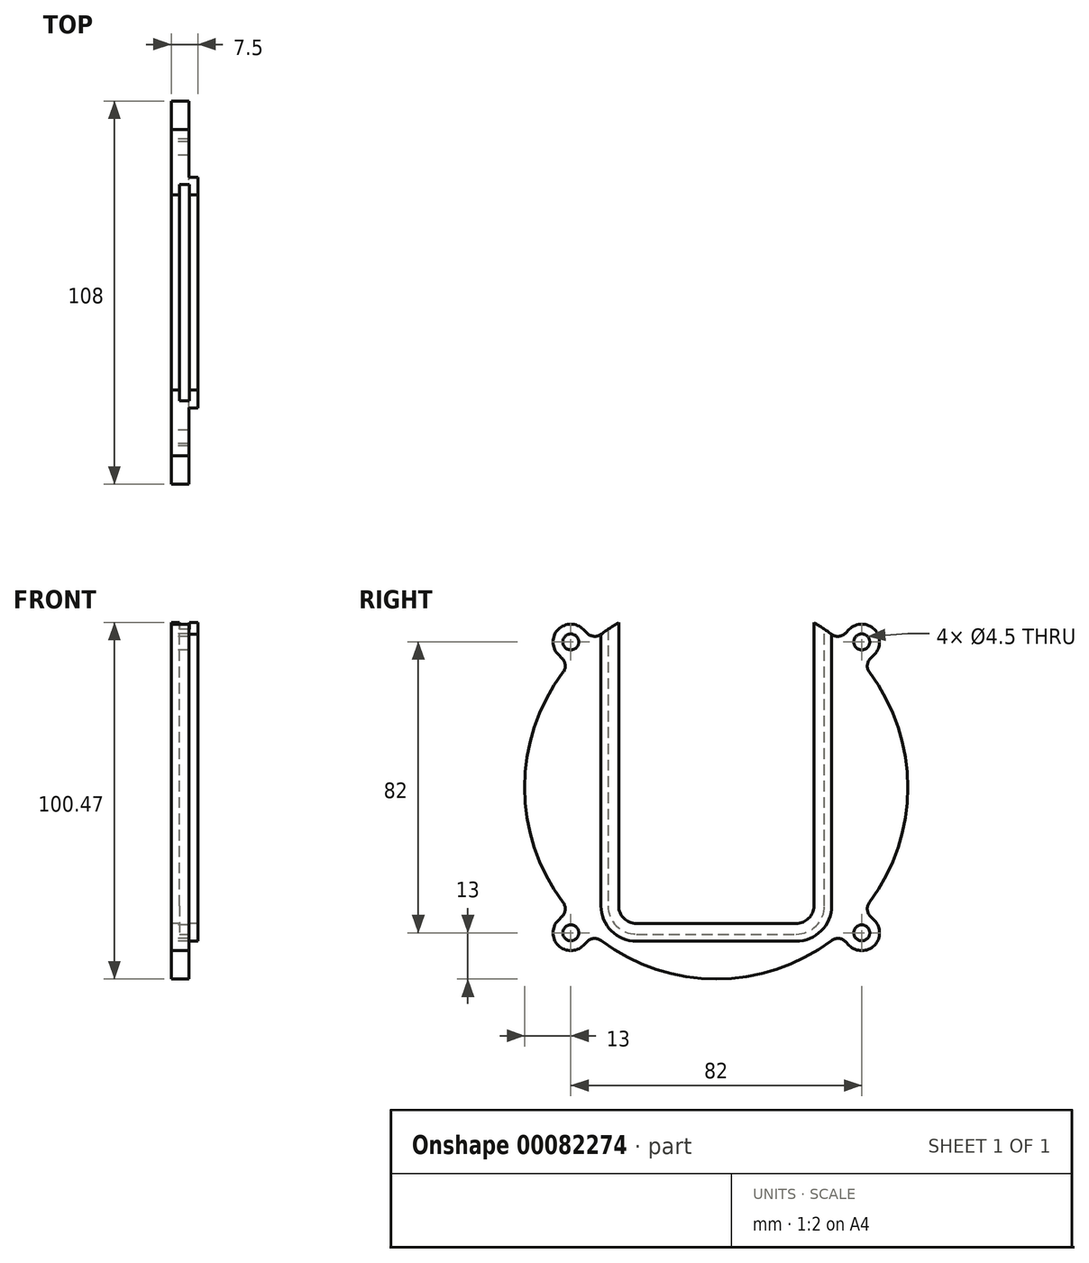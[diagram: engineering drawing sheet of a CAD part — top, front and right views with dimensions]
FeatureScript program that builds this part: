
annotation { "Feature Type Name" : "Feature", "Feature Type Description" : "" }
export const myFeature = defineFeature(function(context is Context, id is Id, definition is map)
    precondition{}
    {
        {
            var Q0;
            Q0=qCreatedBy(makeId("Right.planeOp"),FACE);
            var sketch = newSketch(context, id + "F0", { "sketchPlane" : qUnion([Q0])});
            skCircle(sketch, "E0", {"center": v(-41, 41) * mm, "radius": 2.25 * mm});
            skCircle(sketch, "E1", {"center": v(41, 41) * mm, "radius": 2.25 * mm});
            skCircle(sketch, "E2", {"center": v(41, -41) * mm, "radius": 2.25 * mm});
            skCircle(sketch, "E3", {"center": v(-41, -41) * mm, "radius": 2.25 * mm});
            skArc(sketch, "E4", {"start": v(-32.45, 43.16) * mm, "mid": v(-24.12, -48.31) * mm, "end": v(54, 0) * mm});
            skArc(sketch, "E5", {"start": v(37.46, -44.54) * mm, "mid": v(44.54, -44.54) * mm, "end": v(44.54, -37.46) * mm});
            skArc(sketch, "E6", {"start": v(-44.54, -37.46) * mm, "mid": v(-44.54, -44.54) * mm, "end": v(-37.46, -44.54) * mm});
            skLineSegment(sketch, "E7", {"start": v(-44.54, 37.46) * mm, "end": v(-36.42, 45.58) * mm, "construction": true});
            skLineSegment(sketch, "E8", {"start": v(-44.54, 37.46) * mm, "end": v(-43.44, 36.37) * mm});
            skLineSegment(sketch, "E9", {"start": v(-37.46, 44.54) * mm, "end": v(-36.37, 43.44) * mm});
            skLineSegment(sketch, "E10", {"start": v(37.46, 44.54) * mm, "end": v(46.12, 35.88) * mm, "construction": true});
            skLineSegment(sketch, "E11", {"start": v(37.46, 44.54) * mm, "end": v(36.37, 43.44) * mm});
            skLineSegment(sketch, "E12", {"start": v(44.54, 37.46) * mm, "end": v(43.44, 36.37) * mm});
            skLineSegment(sketch, "E13", {"start": v(-44.54, -37.46) * mm, "end": v(-35.54, -46.46) * mm, "construction": true});
            skLineSegment(sketch, "E14", {"start": v(-44.54, -37.46) * mm, "end": v(-43.44, -36.37) * mm});
            skLineSegment(sketch, "E15", {"start": v(-37.46, -44.54) * mm, "end": v(-36.37, -43.44) * mm});
            skLineSegment(sketch, "E16", {"start": v(37.46, -44.54) * mm, "end": v(47.36, -34.64) * mm, "construction": true});
            skLineSegment(sketch, "E17", {"start": v(37.46, -44.54) * mm, "end": v(36.37, -43.44) * mm});
            skLineSegment(sketch, "E18", {"start": v(44.54, -37.46) * mm, "end": v(43.44, -36.37) * mm});
            skArc(sketch, "E19.trimOffspring", {"start": v(-37.46, 44.54) * mm, "mid": v(-44.54, 44.54) * mm, "end": v(-44.54, 37.46) * mm});
            skArc(sketch, "E20.trimOffspring", {"start": v(32.45, 43.16) * mm, "mid": v(30.02, 44.89) * mm, "end": v(27.5, 46.47) * mm});
            skArc(sketch, "E21.trimOffspring", {"start": v(44.54, 37.46) * mm, "mid": v(44.54, 44.54) * mm, "end": v(37.46, 44.54) * mm});
            skArc(sketch, "E22.trimOffspring", {"start": v(-32.45, -43.16) * mm, "mid": v(0, -54) * mm, "end": v(32.45, -43.16) * mm});
            skPoint(sketch, "E23.visualSharp", {"position": v(-41.56, 34.48) * mm});
            skPoint(sketch, "E24.visualSharp", {"position": v(-34.48, 41.56) * mm});
            skArc(sketch, "E24.filletArc", {"start": v(-36.37, 43.44) * mm, "mid": v(-34.46, 42.57) * mm, "end": v(-32.45, 43.16) * mm});
            skPoint(sketch, "E25.visualSharp", {"position": v(-41.56, -34.48) * mm});
            skArc(sketch, "E25.filletArc", {"start": v(-43.44, -36.37) * mm, "mid": v(-42.57, -34.46) * mm, "end": v(-43.16, -32.45) * mm});
            skPoint(sketch, "E26.visualSharp", {"position": v(-34.48, -41.56) * mm});
            skArc(sketch, "E26.filletArc", {"start": v(-32.45, -43.16) * mm, "mid": v(-34.46, -42.57) * mm, "end": v(-36.37, -43.44) * mm});
            skPoint(sketch, "E27.visualSharp", {"position": v(41.56, -34.48) * mm});
            skArc(sketch, "E27.filletArc", {"start": v(43.16, -32.45) * mm, "mid": v(42.57, -34.46) * mm, "end": v(43.44, -36.37) * mm});
            skPoint(sketch, "E28.visualSharp", {"position": v(34.48, -41.56) * mm});
            skArc(sketch, "E28.filletArc", {"start": v(36.37, -43.44) * mm, "mid": v(34.46, -42.57) * mm, "end": v(32.45, -43.16) * mm});
            skPoint(sketch, "E29.visualSharp", {"position": v(41.56, 34.48) * mm});
            skArc(sketch, "E29.filletArc", {"start": v(43.44, 36.37) * mm, "mid": v(42.57, 34.46) * mm, "end": v(43.16, 32.45) * mm});
            skPoint(sketch, "E30.visualSharp", {"position": v(34.48, 41.56) * mm});
            skArc(sketch, "E30.filletArc", {"start": v(32.45, 43.16) * mm, "mid": v(34.46, 42.57) * mm, "end": v(36.37, 43.44) * mm});
            skArc(sketch, "E31.filletArc", {"start": v(-43.16, 32.45) * mm, "mid": v(-42.57, 34.46) * mm, "end": v(-43.44, 36.37) * mm});
            skArc(sketch, "E32.converted", {"start": v(-27.5, 46.47) * mm, "mid": v(0, -54) * mm, "end": v(27.5, 46.47) * mm});
            skLineSegment(sketch, "E33", {"start": v(-27.5, 46.47) * mm, "end": v(-27.5, -33.36) * mm});
            skLineSegment(sketch, "E34", {"start": v(27.5, 46.47) * mm, "end": v(27.5, -33.36) * mm});
            skCircle(sketch, "E35", {"center": v(0, 0) * mm, "radius": 17.5 * mm, "construction": true});
            skCircle(sketch, "E36", {"center": v(20.15, 20.15) * mm, "radius": 2.25 * mm, "construction": true});
            skCircle(sketch, "E37", {"center": v(-20.15, -20.15) * mm, "radius": 2.25 * mm, "construction": true});
            skLineSegment(sketch, "E38.bottom", {"start": v(-26.5, 26.5) * mm, "end": v(26.5, 26.5) * mm, "construction": true});
            skLineSegment(sketch, "E38.top", {"start": v(-26.5, -26.5) * mm, "end": v(26.5, -26.5) * mm, "construction": true});
            skLineSegment(sketch, "E38.left", {"start": v(-26.5, 26.5) * mm, "end": v(-26.5, -26.5) * mm, "construction": true});
            skLineSegment(sketch, "E38.right", {"start": v(26.5, 26.5) * mm, "end": v(26.5, -26.5) * mm, "construction": true});
            skArc(sketch, "E39.trimOffspring", {"start": v(-21.68, -18.5) * mm, "mid": v(-20.15, -20.15) * mm, "end": v(-18.5, -21.68) * mm, "construction": true});
            skArc(sketch, "E40.trimOffspring", {"start": v(21.68, 18.5) * mm, "mid": v(20.15, 20.15) * mm, "end": v(18.5, 21.68) * mm, "construction": true});
            skLineSegment(sketch, "E41", {"start": v(-22.5, -38.36) * mm, "end": v(22.5, -38.36) * mm});
            skPoint(sketch, "E42.orphan", {"position": v(-27.5, -21.94) * mm});
            skPoint(sketch, "E43.orphan", {"position": v(27.5, -21.94) * mm});
            skPoint(sketch, "E44.visualSharp", {"position": v(-27.5, -38.36) * mm});
            skArc(sketch, "E44.filletArc", {"start": v(-27.5, -33.36) * mm, "mid": v(-26.04, -36.9) * mm, "end": v(-22.5, -38.36) * mm});
            skPoint(sketch, "E45.visualSharp", {"position": v(27.5, -38.36) * mm});
            skArc(sketch, "E45.filletArc", {"start": v(22.5, -38.36) * mm, "mid": v(26.04, -36.9) * mm, "end": v(27.5, -33.36) * mm});
            skArc(sketch, "E46.trimOffspring", {"start": v(-27.5, 46.47) * mm, "mid": v(-30.02, 44.89) * mm, "end": v(-32.45, 43.16) * mm});
            skPoint(sketch, "E47.orphan", {"position": v(-27.5, 53.27) * mm});
            skPoint(sketch, "E48.orphan", {"position": v(27.5, 53.27) * mm});
            skLineSegment(sketch, "E49", {"start": v(-32.5, 43.12) * mm, "end": v(-32.5, -33.36) * mm});
            skLineSegment(sketch, "E50", {"start": v(-22.5, -43.36) * mm, "end": v(22.5, -43.36) * mm});
            skLineSegment(sketch, "E51", {"start": v(32.5, -33.36) * mm, "end": v(32.5, 43.12) * mm});
            skPoint(sketch, "E52.visualSharp", {"position": v(-32.5, -43.36) * mm});
            skArc(sketch, "E52.filletArc", {"start": v(-32.5, -33.36) * mm, "mid": v(-29.57, -40.43) * mm, "end": v(-22.5, -43.36) * mm});
            skPoint(sketch, "E53.visualSharp", {"position": v(32.5, -43.36) * mm});
            skArc(sketch, "E53.filletArc", {"start": v(22.5, -43.36) * mm, "mid": v(29.57, -40.43) * mm, "end": v(32.5, -33.36) * mm});
            skSolve(sketch);
        }
        {
            var Q0;
            {var subQ4=sQuery(id+"F0.wireOp",EDGE,"E49");Q0=makeQuery(id+"F0.imprint","IMPRINT",FACE,{"disambiguationData":[TD([[makeQuery(id+"F0.imprint","IMPRINT",EDGE,{"derivedFrom":subQ4}),-1.0]])]});}
            var Q1;
            Q1=makeQuery(id+"F0.imprint","IMPRINT",FACE,{"disambiguationData":[TD([[makeQuery(id+"F0.imprint","IMPRINT",EDGE,{"derivedFrom":sQuery(id+"F0.wireOp",EDGE,"E0")}),-1.0]])]});
            var Q2;
            Q2=makeQuery(id+"F0.imprint","IMPRINT",FACE,{"disambiguationData":[TD([[makeQuery(id+"F0.imprint","IMPRINT",EDGE,{"derivedFrom":sQuery(id+"F0.wireOp",EDGE,"E1")}),-1.0]])]});
            var Q3;
            Q3=makeQuery(id+"F0.imprint","IMPRINT",FACE,{"disambiguationData":[TD([[makeQuery(id+"F0.imprint","IMPRINT",EDGE,{"derivedFrom":sQuery(id+"F0.wireOp",EDGE,"E2")}),-1.0]])]});
            var Q4;
            Q4=makeQuery(id+"F0.imprint","IMPRINT",FACE,{"disambiguationData":[TD([[makeQuery(id+"F0.imprint","IMPRINT",EDGE,{"derivedFrom":sQuery(id+"F0.wireOp",EDGE,"E3")}),-1.0]])]});
            extrude(context, id + "F1", {"entities" : qUnion([Q0, Q1, Q2, Q3, Q4]), "depth" : 5 * mm, "offsetDistance" : 25 * mm});
        }
        {
            var Q0;
            Q0=makeQuery(id+"F0.imprint","IMPRINT",FACE,{"disambiguationData":[TD([[makeQuery(id+"F0.imprint","IMPRINT",EDGE,{"derivedFrom":sQuery(id+"F0.wireOp",EDGE,"E33")}),-1.0]])]});
            extrude(context, id + "F2", {"entities" : qUnion([Q0]), "operationType" : NewBodyOperationType.ADD, "depth" : 7.5 * mm, "offsetDistance" : 25 * mm});
        }
        {
            var Q0;
            Q0=qCreatedBy(makeId("Top.planeOp"),FACE);
            var Q1;
            Q1=sQuery(id+"F0.wireOp",VERTEX,"E32.converted.start");
            cPlane(context, id + "F3", {"entities" : qUnion([Q0, Q1]), "cplaneType" : CPlaneType.PLANE_POINT, "offset" : 30.6 * mm, "width" : 150 * mm, "height" : 150 * mm});
        }
        {
            var Q0;
            Q0=qCreatedBy(id+"F3.planeOp",FACE);
            var sketch = newSketch(context, id + "F4", { "sketchPlane" : qUnion([Q0])});
            skLineSegment(sketch, "E54.bottom", {"start": v(2.38, -30.5) * mm, "end": v(5.12, -30.5) * mm});
            skLineSegment(sketch, "E54.top", {"start": v(2.37, -25.5) * mm, "end": v(5.12, -25.5) * mm});
            skLineSegment(sketch, "E54.left", {"start": v(2.38, -30.5) * mm, "end": v(2.37, -25.5) * mm});
            skLineSegment(sketch, "E54.right", {"start": v(5.12, -30.5) * mm, "end": v(5.12, -25.5) * mm});
            skSolve(sketch);
        }
        {
            var Q0;
            Q0=makeQuery(id+"F4.imprint","IMPRINT",FACE,{"disambiguationData":[TD([[makeQuery(id+"F4.imprint","IMPRINT",EDGE,{"derivedFrom":sQuery(id+"F4.wireOp",EDGE,"E54.bottom")}),1.0]])]});
            var Q1;
            Q1=sQuery(id+"F0.wireOp",EDGE,"E33");
            var Q2;
            Q2=sQuery(id+"F0.wireOp",EDGE,"E44.filletArc");
            var Q3;
            Q3=sQuery(id+"F0.wireOp",EDGE,"E41");
            var Q4;
            Q4=sQuery(id+"F0.wireOp",EDGE,"E45.filletArc");
            var Q5;
            Q5=sQuery(id+"F0.wireOp",EDGE,"E34");
            sweep(context, id + "F5", {"operationType" : NewBodyOperationType.REMOVE, "profiles" : qUnion([Q0]), "path" : qUnion([Q1, Q2, Q3, Q4, Q5])});
        }
    });
